# Revit family: DF_МуфтаСоединительная_EZETEK
name_source: partatom
category: Соединительные детали воздуховодов
revit_build: Autodesk Revit 2017 (Build: 20170118_1100(x64)
units: mm (PartAtom-declared; Revit-internal decimal feet)

## family parameters
Всегда вертикально = Да
На основе рабочей плоскости = Нет
Общий = Нет
При загрузке вырезать с полостями = Нет
Размер круглого соединителя = Использовать радиус
Тип детали = Соединение

## types (4) — shared parameters
ADSK_Версия Revit = 2017
ADSK_Единица измерения = Неспецифицируемое
ADSK_Завод-изготовитель = Неспецифицируемое
ADSK_Код изделия = Неспецифицируемое
ADSK_Марка = Неспецифицируемое
ADSK_Масса_Текст = Неспецифицируемое
ADSK_Наименование = Неспецифицируемое
ADSK_Обозначение = Неспецифицируемое
URL = https://ezetek.ru
Группа модели = Муфты соединительные
Изготовитель = Ezetek
Описание = При монтаже стержни заземления соприкасаются друг с другом в центре муфты, благодаря чему ударный импульс не «рассеивается» и с муфты снимается механическая нагрузка.
Угол = 90.00°
zero-valued in all types: ADSK_Количество, ADSK_Масса

## per-type parameters (varying)
| type | ADSK_Материал | Тип |
| МуфтаСоединительная_Латунь | BIMLIB_Латунь_EZETEK | FA_МуфтаСоединительная_EZETEK : МуфтаСоединительная_Латунь |
| МуфтаСоединительная_Сталь_Нержавеющая | BIMLIB_Сталь_Нержавеющая_EZETEK | FA_МуфтаСоединительная_EZETEK : МуфтаСоединительная_Сталь_Нержавеющая |
| МуфтаСоединительная_Сталь_Оцинкованная | BIMLIB_Сталь_Оцинкованная_EZETEK | FA_МуфтаСоединительная_EZETEK : МуфтаСоединительная_Сталь_Оцинкованная |
| МуфтаСоединительная_Сталь_ГорОцинкованная | BIMLIB_Сталь_Оцинкованная_EZETEK | FA_МуфтаСоединительная_EZETEK : МуфтаСоединительная_Сталь_ГорОцинкованная |
